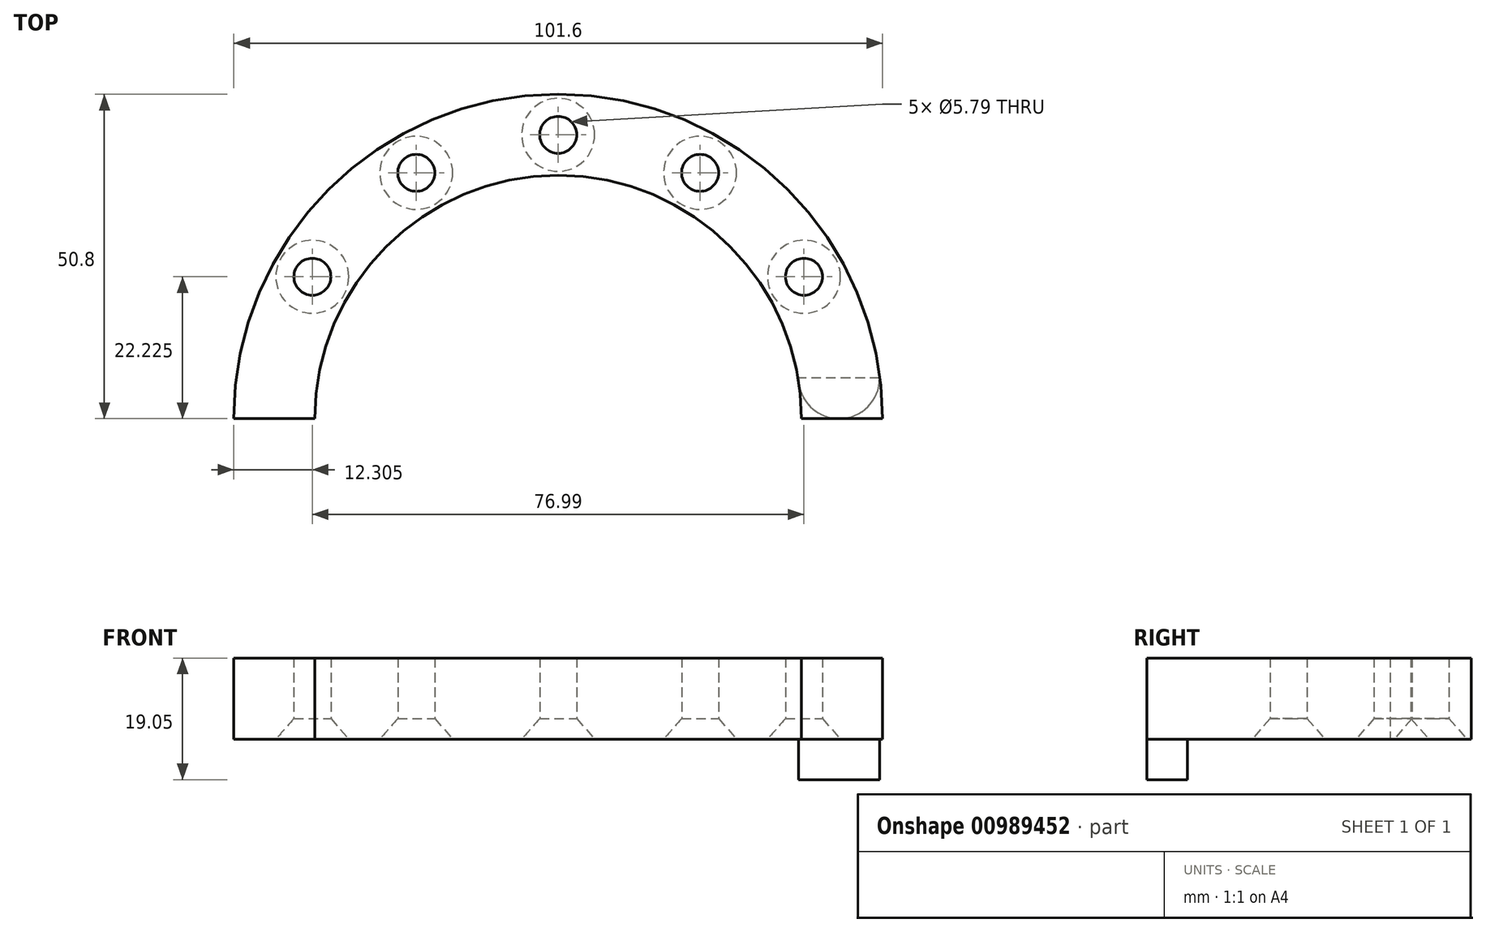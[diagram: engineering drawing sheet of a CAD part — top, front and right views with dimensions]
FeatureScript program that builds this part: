
annotation { "Feature Type Name" : "Feature", "Feature Type Description" : "" }
export const myFeature = defineFeature(function(context is Context, id is Id, definition is map)
    precondition{}
    {
        {
            var Q0;
            Q0=qCreatedBy(makeId("Top.planeOp"),FACE);
            var sketch = newSketch(context, id + "F0", { "sketchPlane" : qUnion([Q0])});
            skArc(sketch, "E0", {"start": v(-50.8, 0) * mm, "mid": v(0, 50.8) * mm, "end": v(50.8, 0) * mm});
            skArc(sketch, "E1", {"start": v(-38.1, 0) * mm, "mid": v(0, 38.1) * mm, "end": v(38.1, 0) * mm});
            skLineSegment(sketch, "E2", {"start": v(-50.8, 0) * mm, "end": v(-38.1, 0) * mm});
            skLineSegment(sketch, "E3", {"start": v(38.1, 0) * mm, "end": v(50.8, 0) * mm});
            skSolve(sketch);
        }
        {
            var Q0;
            Q0 = qSketchRegion(id + "F0", true);
            extrude(context, id + "F1", {"entities" : qUnion([Q0]), "depth" : 12.7 * mm, "offsetDistance" : 25.4 * mm});
        }
        {
            var Q0;
            Q0=qCreatedBy(makeId("Top.planeOp"),FACE);
            var sketch = newSketch(context, id + "F2", { "sketchPlane" : qUnion([Q0])});
            skArc(sketch, "E4", {"start": v(37.64, 6.35) * mm, "mid": v(44, 0) * mm, "end": v(50.34, 6.35) * mm});
            skLineSegment(sketch, "E5", {"start": v(44, 6.35) * mm, "end": v(37.64, 6.35) * mm});
            skLineSegment(sketch, "E6", {"start": v(44, 6.35) * mm, "end": v(50.34, 6.35) * mm});
            skLineSegment(sketch, "E7", {"start": v(0, 0) * mm, "end": v(0, 57.22) * mm, "construction": true});
            skArc(sketch, "E8.MirrorCS", {"start": v(-37.64, 6.35) * mm, "mid": v(-44, 0) * mm, "end": v(-50.34, 6.35) * mm});
            skLineSegment(sketch, "E9.MirrorCS", {"start": v(-44, 6.35) * mm, "end": v(-37.64, 6.35) * mm});
            skLineSegment(sketch, "E10.MirrorCS", {"start": v(-44, 6.35) * mm, "end": v(-50.34, 6.35) * mm});
            skSolve(sketch);
        }
        {
            var Q0;
            Q0=makeQuery(id+"F2.imprint","IMPRINT",FACE,{"disambiguationData":[TD([[makeQuery(id+"F2.imprint","IMPRINT",EDGE,{"derivedFrom":sQuery(id+"F2.wireOp",EDGE,"E4")}),1.0]])]});
            var Q1;
            Q1=makeQuery(id+"F2.imprint","IMPRINT",FACE,{"disambiguationData":[TD([[makeQuery(id+"F2.imprint","IMPRINT",EDGE,{"derivedFrom":sQuery(id+"F2.wireOp",EDGE,"E8.MirrorCS")}),-1.0]])]});
            extrude(context, id + "F3", {"entities" : qUnion([Q0, Q1]), "operationType" : NewBodyOperationType.ADD, "oppositeDirection" : true, "depth" : 6.35 * mm, "offsetDistance" : 25.4 * mm});
        }
        {
            var Q0;
            Q0=qCreatedBy(makeId("Top.planeOp"),FACE);
            var sketch = newSketch(context, id + "F4", { "sketchPlane" : qUnion([Q0])});
            skArc(sketch, "E11", {"start": v(44.45, 0) * mm, "mid": v(0, 44.45) * mm, "end": v(-44.45, 0) * mm, "construction": true});
            skPoint(sketch, "E12", {"position": v(-44.45, 0) * mm});
            skPoint(sketch, "E13.1.0", {"position": v(-38.5, 22.23) * mm});
            skPoint(sketch, "E13.2.0", {"position": v(-22.23, 38.5) * mm});
            skPoint(sketch, "E13.3.0", {"position": v(0, 44.45) * mm});
            skPoint(sketch, "E13.4.0", {"position": v(22.22, 38.5) * mm});
            skPoint(sketch, "E13.5.0", {"position": v(38.5, 22.22) * mm});
            skPoint(sketch, "E13.6.0", {"position": v(44.45, 0) * mm});
            skLineSegment(sketch, "E13.anchor1", {"start": v(0, 0) * mm, "end": v(-44.45, 0) * mm, "construction": true});
            skLineSegment(sketch, "E13.anchor2", {"start": v(0, 0) * mm, "end": v(44.45, 0) * mm, "construction": true});
            skSolve(sketch);
        }
        {
            var Q0;
            Q0=sQuery(id+"F4.wireOp",VERTEX,"E13.1.0");
            var Q1;
            Q1=sQuery(id+"F4.wireOp",VERTEX,"E13.2.0");
            var Q2;
            Q2=sQuery(id+"F4.wireOp",VERTEX,"E13.3.0");
            var Q3;
            Q3=sQuery(id+"F4.wireOp",VERTEX,"E13.4.0");
            var Q4;
            Q4=sQuery(id+"F4.wireOp",VERTEX,"E13.5.0");
            var Q5;
            Q5=makeQuery(id+"F1.opExtrude","SWEPT_BODY",BODY,{"disambiguationData":[OSD([sQuery(id+"F0.wireOp",EDGE,"E0"),sQuery(id+"F0.wireOp",EDGE,"E1"),sQuery(id+"F0.wireOp",EDGE,"E2"),sQuery(id+"F0.wireOp",EDGE,"E3")])]});
            hole(context, id + "F5", {"style" : HoleStyle.C_SINK, "endStyle" : HoleEndStyle.THROUGH, "oppositeDirection" : true, "standardTappedOrClearance" : lookupTablePath({ "fit" : "Free", "standard" : "ANSI", "size" : "#12", "type" : "Clearance" }), "standardBlindInLast" : lookupTablePath({ "fit" : "Normal", "standard" : "ANSI", "engagement" : "75%", "pitch" : "24 tpi", "size" : "#12", "type" : "Clearance & tapped" }), "holeDiameter" : 5.8 * mm, "cSinkDiameter" : 11.43 * mm, "cSinkAngle" : 82 * degree, "majorDiameter" : 6.35 * mm, "isTappedThrough" : true, "tappedDepth" : 12.7 * mm, "tapClearance" : 3, "locations" : qUnion([Q0, Q1, Q2, Q3, Q4]), "scope" : qUnion([Q5])});
        }
    });
